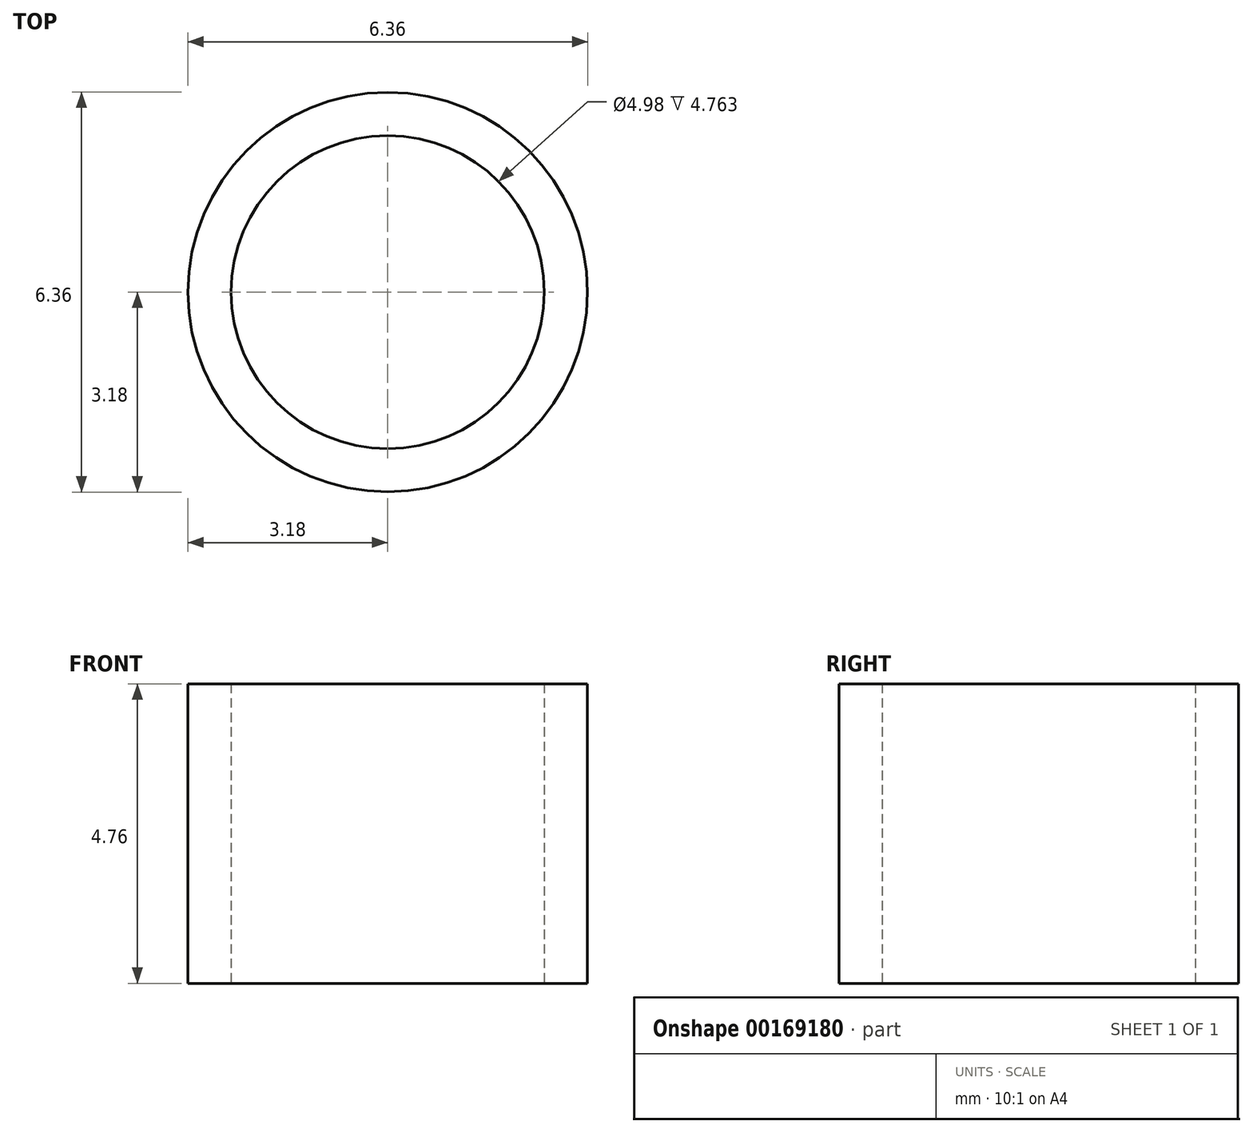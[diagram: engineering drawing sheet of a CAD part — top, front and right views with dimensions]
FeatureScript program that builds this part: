
annotation { "Feature Type Name" : "Feature", "Feature Type Description" : "" }
export const myFeature = defineFeature(function(context is Context, id is Id, definition is map)
    precondition{}
    {
        {
            var Q0;
            Q0=qCreatedBy(makeId("Top.planeOp"),FACE);
            var sketch = newSketch(context, id + "F0", { "sketchPlane" : qUnion([Q0])});
            skCircle(sketch, "E0", {"center": v(0, 0) * mm, "radius": 3.18 * mm});
            skSolve(sketch);
        }
        {
            var Q0;
            Q0 = qSketchRegion(id + "F0", true);
            extrude(context, id + "F1", {"entities" : qUnion([Q0]), "depth" : 4.76 * mm});
        }
        {
            var Q0;
            Q0=sQuery(id+"F0.wireOp",VERTEX,"E0.center");
            var Q1;
            Q1=makeQuery(id+"F1.opExtrude","SWEPT_BODY",BODY,{"disambiguationData":[OSD([sQuery(id+"F0.wireOp",EDGE,"E0")])]});
            hole(context, id + "F2", {"style" : HoleStyle.SIMPLE, "endStyle" : HoleEndStyle.THROUGH, "oppositeDirection" : true, "standardTappedOrClearance" : lookupTablePath({ "standard" : "ANSI", "fit" : "Close", "size" : "#10", "type" : "Clearance" }), "standardBlindInLast" : lookupTablePath({ "fit" : "Close", "standard" : "ANSI", "size" : "#10", "type" : "Clearance" }), "holeDiameter" : 4.98 * mm, "startFromSketch" : true, "locations" : qUnion([Q0]), "scope" : qUnion([Q1]), "isTappedThrough" : true});
        }
    });
